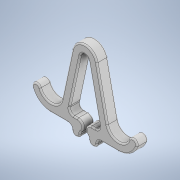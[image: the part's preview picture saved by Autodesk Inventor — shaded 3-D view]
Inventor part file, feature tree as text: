
AUTODESK INVENTOR PART (.ipt)
format: ipt  version: 2020 (Build 240168000, 168)  size: 320,512 bytes
history: native  units: in
note: dims shown in document units (in); Inventor stores cm internally (conversion verified against a paired STEP export)
features: extrude x2, sketch x2, fillet x1, projected_geometry x1
ambient origin geometry x8: Origin, YZ Plane, XZ Plane, XY Plane, X Axis, Y Axis, Z Axis, Center Point
bodies: Body1 (feature_tree)
feature tree (6):
  extrude  "Extrusion2"  Depth=3.0in
  extrude  "Extrusion3"  Depth=0.0625in
  fillet  "Fillet2"  Radius=1.0994in
  sketch  "Sketch2"  dims[d18=0.375in d19=3.0in]
  sketch  "Sketch4"  dims[d20=3.0in d21=1.0in d23=1.0994in d24=1.0994in d25=0.5in d26=0.0in d30=0.0in d31=0.0in d32=0.5in d33=0.0625in]
  projected_geometry  "Projected Loop1"
